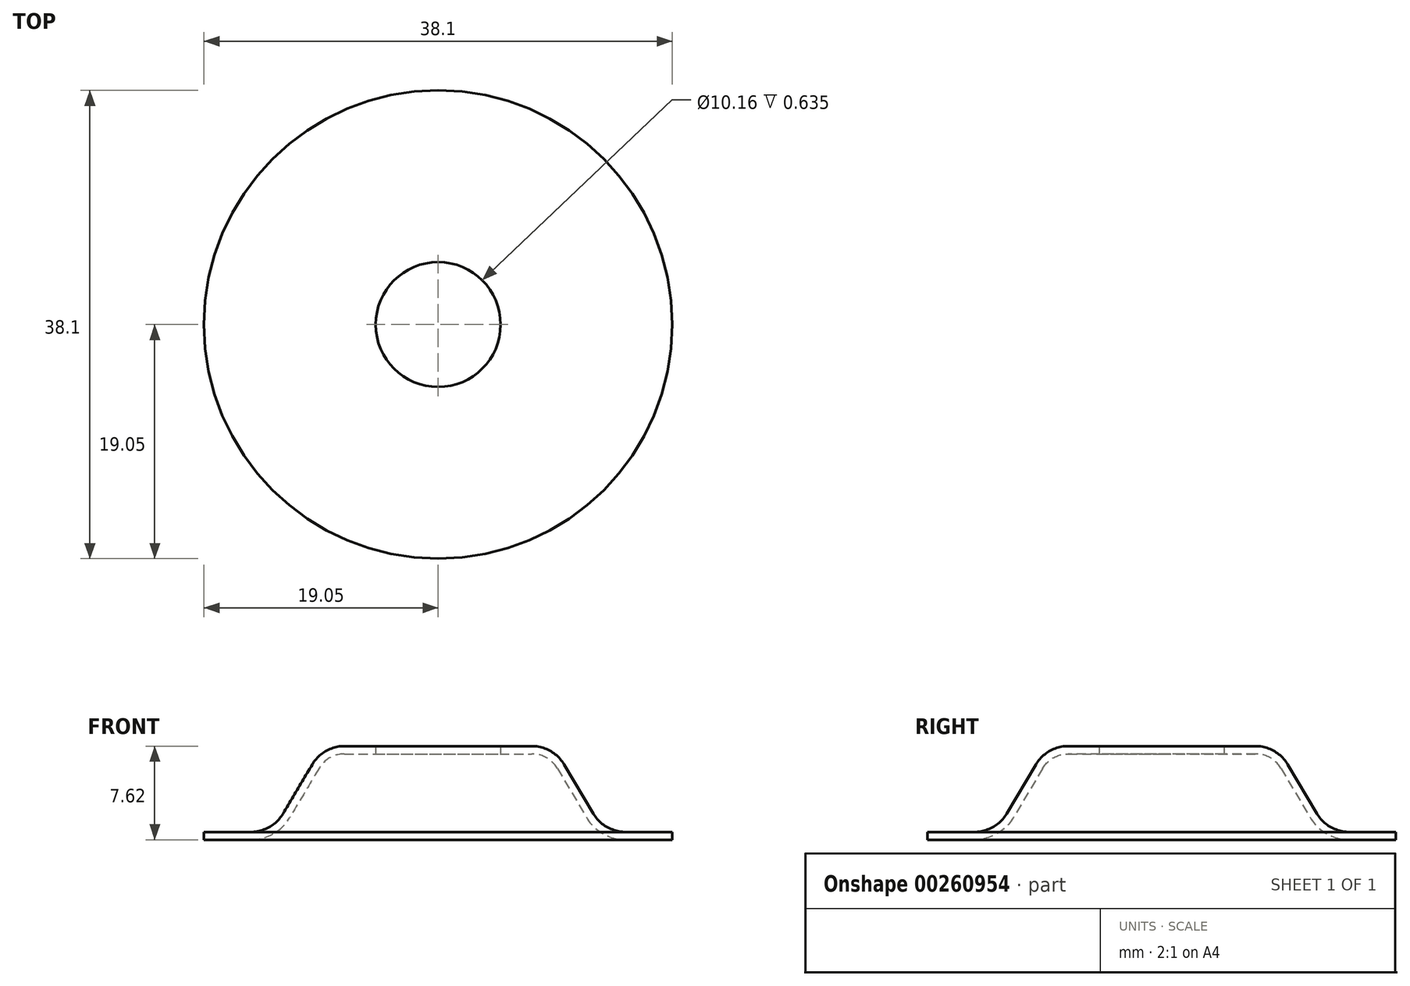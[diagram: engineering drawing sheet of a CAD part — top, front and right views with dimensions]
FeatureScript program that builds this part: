
annotation { "Feature Type Name" : "Feature", "Feature Type Description" : "" }
export const myFeature = defineFeature(function(context is Context, id is Id, definition is map)
    precondition{}
    {
        {
            var Q0;
            Q0=qCreatedBy(makeId("Front.planeOp"),FACE);
            var sketch = newSketch(context, id + "F0", { "sketchPlane" : qUnion([Q0])});
            skLineSegment(sketch, "E0", {"start": v(5.08, 7.62) * mm, "end": v(7.62, 7.62) * mm});
            skLineSegment(sketch, "E1", {"start": v(10.24, 6.13) * mm, "end": v(12.62, 2.13) * mm});
            skLineSegment(sketch, "E2", {"start": v(15.24, 0.64) * mm, "end": v(19.05, 0.64) * mm});
            skPoint(sketch, "E3.visualSharp", {"position": v(9.35, 7.62) * mm});
            skArc(sketch, "E3.filletArc", {"start": v(10.24, 6.13) * mm, "mid": v(9.13, 7.22) * mm, "end": v(7.62, 7.62) * mm});
            skPoint(sketch, "E4.visualSharp", {"position": v(13.5, 0.64) * mm});
            skArc(sketch, "E4.filletArc", {"start": v(12.62, 2.13) * mm, "mid": v(13.73, 1.03) * mm, "end": v(15.24, 0.64) * mm});
            skLineSegment(sketch, "E5.0", {"start": v(15.24, 0) * mm, "end": v(19.05, 0) * mm});
            skLineSegment(sketch, "E5.1", {"start": v(5.08, 6.98) * mm, "end": v(7.62, 6.98) * mm});
            skArc(sketch, "E5.2", {"start": v(9.7, 5.8) * mm, "mid": v(8.81, 6.67) * mm, "end": v(7.62, 6.99) * mm});
            skLineSegment(sketch, "E5.3", {"start": v(9.7, 5.8) * mm, "end": v(12.07, 1.8) * mm});
            skArc(sketch, "E5.4", {"start": v(12.07, 1.8) * mm, "mid": v(13.42, 0.48) * mm, "end": v(15.24, 0) * mm});
            skLineSegment(sketch, "E6", {"start": v(5.08, 7.62) * mm, "end": v(5.08, 6.98) * mm});
            skLineSegment(sketch, "E7", {"start": v(19.05, 0.64) * mm, "end": v(19.05, 0) * mm});
            skLineSegment(sketch, "E8", {"start": v(0, -25.22) * mm, "end": v(0, 31.27) * mm, "construction": true});
            skLineSegment(sketch, "E9", {"start": v(0, 0) * mm, "end": v(33.95, 0) * mm, "construction": true});
            skSolve(sketch);
        }
        {
            var Q0;
            Q0=makeQuery(id+"F0.imprint","IMPRINT",FACE,{"disambiguationData":[TD([[makeQuery(id+"F0.imprint","IMPRINT",EDGE,{"derivedFrom":sQuery(id+"F0.wireOp",EDGE,"E0")}),-1.0]])]});
            var Q1;
            Q1=sQuery(id+"F0.wireOp",EDGE,"E8");
            revolve(context, id + "F1", {"entities" : qUnion([Q0]), "axis" : qUnion([Q1]), "revolveType" : RevolveType.FULL});
        }
    });
